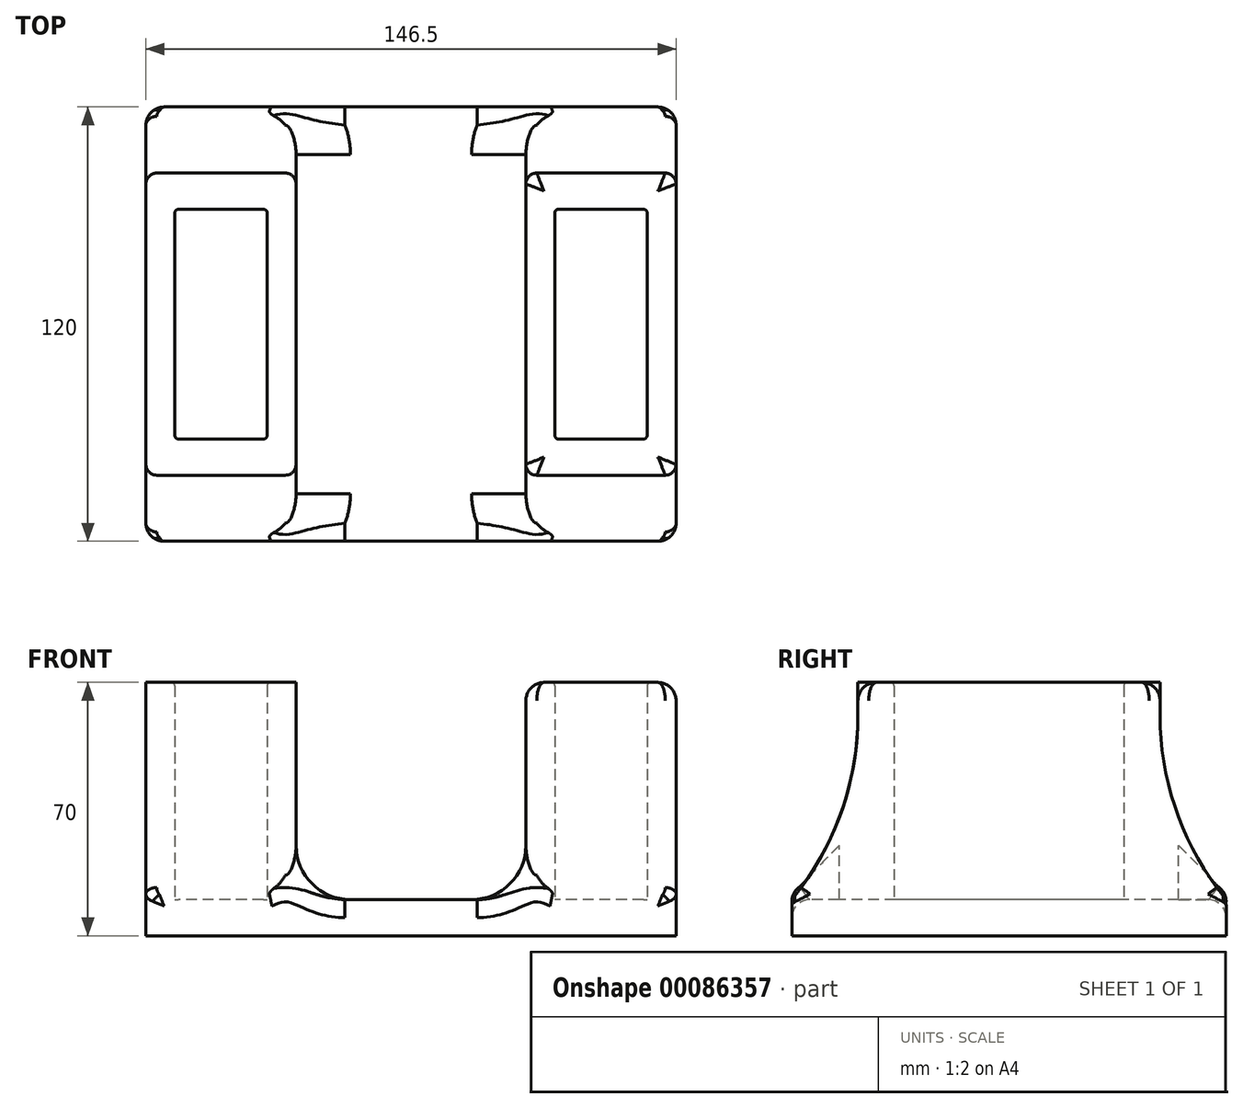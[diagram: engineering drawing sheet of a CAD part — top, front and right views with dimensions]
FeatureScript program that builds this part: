
annotation { "Feature Type Name" : "Feature", "Feature Type Description" : "" }
export const myFeature = defineFeature(function(context is Context, id is Id, definition is map)
    precondition{}
    {
        {
            var Q0;
            Q0=qCreatedBy(makeId("Top.planeOp"),FACE);
            var sketch = newSketch(context, id + "F0", { "sketchPlane" : qUnion([Q0])});
            skLineSegment(sketch, "E0.bottom", {"start": v(73.25, 60) * mm, "end": v(-73.25, 60) * mm});
            skLineSegment(sketch, "E0.top", {"start": v(73.25, -60) * mm, "end": v(-73.25, -60) * mm});
            skLineSegment(sketch, "E0.left", {"start": v(73.25, 60) * mm, "end": v(73.25, -60) * mm});
            skLineSegment(sketch, "E0.right", {"start": v(-73.25, 60) * mm, "end": v(-73.25, -60) * mm});
            skPoint(sketch, "E0.middle", {"position": v(0, 0) * mm});
            skLineSegment(sketch, "E1", {"start": v(-73.25, 0) * mm, "end": v(-52.5, 0) * mm});
            skPoint(sketch, "E1.endSnap0", {"position": v(-73.25, 0) * mm});
            skLineSegment(sketch, "E2", {"start": v(-52.5, 0) * mm, "end": v(52.5, 0) * mm});
            skPoint(sketch, "E2.endSnap0", {"position": v(73.25, 0) * mm});
            skLineSegment(sketch, "E3", {"start": v(52.5, 0) * mm, "end": v(73.25, 0) * mm});
            skLineSegment(sketch, "E4.bottom", {"start": v(-73.25, 41.75) * mm, "end": v(-31.75, 41.75) * mm});
            skLineSegment(sketch, "E4.top", {"start": v(-73.25, -41.75) * mm, "end": v(-31.75, -41.75) * mm});
            skLineSegment(sketch, "E4.left", {"start": v(-73.25, 41.75) * mm, "end": v(-73.25, -41.75) * mm});
            skLineSegment(sketch, "E4.right", {"start": v(-31.75, 41.75) * mm, "end": v(-31.75, -41.75) * mm});
            skPoint(sketch, "E4.middle", {"position": v(-52.5, 0) * mm});
            skLineSegment(sketch, "E5.bottom", {"start": v(73.25, 41.75) * mm, "end": v(31.75, 41.75) * mm});
            skLineSegment(sketch, "E5.top", {"start": v(73.25, -41.75) * mm, "end": v(31.75, -41.75) * mm});
            skLineSegment(sketch, "E5.left", {"start": v(73.25, 41.75) * mm, "end": v(73.25, -41.75) * mm});
            skLineSegment(sketch, "E5.right", {"start": v(31.75, 41.75) * mm, "end": v(31.75, -41.75) * mm});
            skPoint(sketch, "E5.middle", {"position": v(52.5, 0) * mm});
            skLineSegment(sketch, "E6.bottom", {"start": v(-39.75, 31.75) * mm, "end": v(-65.25, 31.75) * mm});
            skLineSegment(sketch, "E6.top", {"start": v(-39.75, -31.75) * mm, "end": v(-65.25, -31.75) * mm});
            skLineSegment(sketch, "E6.left", {"start": v(-39.75, 31.75) * mm, "end": v(-39.75, -31.75) * mm});
            skLineSegment(sketch, "E6.right", {"start": v(-65.25, 31.75) * mm, "end": v(-65.25, -31.75) * mm});
            skLineSegment(sketch, "E7.bottom", {"start": v(65.25, 31.75) * mm, "end": v(39.75, 31.75) * mm});
            skLineSegment(sketch, "E7.top", {"start": v(65.25, -31.75) * mm, "end": v(39.75, -31.75) * mm});
            skLineSegment(sketch, "E7.left", {"start": v(65.25, 31.75) * mm, "end": v(65.25, -31.75) * mm});
            skLineSegment(sketch, "E7.right", {"start": v(39.75, 31.75) * mm, "end": v(39.75, -31.75) * mm});
            skSolve(sketch);
        }
        {
            var Q0;
            {var subQ6=sQuery(id+"F0.wireOp",EDGE,"E0.top");Q0=makeQuery(id+"F0.imprint","IMPRINT",FACE,{"disambiguationData":[TD([[makeQuery(id+"F0.imprint","IMPRINT",EDGE,{"derivedFrom":subQ6}),-1.0]])]});}
            var Q1;
            {var subQ6=sQuery(id+"F0.wireOp",EDGE,"E0.bottom");Q1=makeQuery(id+"F0.imprint","IMPRINT",FACE,{"disambiguationData":[TD([[makeQuery(id+"F0.imprint","IMPRINT",EDGE,{"derivedFrom":subQ6}),1.0]])]});}
            var Q2;
            {var subQ3=sQuery(id+"F0.wireOp",EDGE,"E4.bottom");Q2=makeQuery(id+"F0.imprint","IMPRINT",FACE,{"disambiguationData":[TD([[makeQuery(id+"F0.imprint","IMPRINT",EDGE,{"derivedFrom":subQ3}),-1.0]])]});}
            var Q3;
            {var subQ3=sQuery(id+"F0.wireOp",EDGE,"E4.top");Q3=makeQuery(id+"F0.imprint","IMPRINT",FACE,{"disambiguationData":[TD([[makeQuery(id+"F0.imprint","IMPRINT",EDGE,{"derivedFrom":subQ3}),1.0]])]});}
            var Q4;
            {var subQ1=sQuery(id+"F0.wireOp",EDGE,"E6.top");Q4=makeQuery(id+"F0.imprint","IMPRINT",FACE,{"disambiguationData":[TD([[makeQuery(id+"F0.imprint","IMPRINT",EDGE,{"derivedFrom":subQ1}),-1.0]])]});}
            var Q5;
            {var subQ1=sQuery(id+"F0.wireOp",EDGE,"E6.bottom");Q5=makeQuery(id+"F0.imprint","IMPRINT",FACE,{"disambiguationData":[TD([[makeQuery(id+"F0.imprint","IMPRINT",EDGE,{"derivedFrom":subQ1}),1.0]])]});}
            var Q6;
            {var subQ1=sQuery(id+"F0.wireOp",EDGE,"E7.bottom");Q6=makeQuery(id+"F0.imprint","IMPRINT",FACE,{"disambiguationData":[TD([[makeQuery(id+"F0.imprint","IMPRINT",EDGE,{"derivedFrom":subQ1}),1.0]])]});}
            var Q7;
            {var subQ1=sQuery(id+"F0.wireOp",EDGE,"E7.top");Q7=makeQuery(id+"F0.imprint","IMPRINT",FACE,{"disambiguationData":[TD([[makeQuery(id+"F0.imprint","IMPRINT",EDGE,{"derivedFrom":subQ1}),-1.0]])]});}
            var Q8;
            {var subQ0=sQuery(id+"F0.wireOp",EDGE,"E5.top");Q8=makeQuery(id+"F0.imprint","IMPRINT",FACE,{"disambiguationData":[TD([[makeQuery(id+"F0.imprint","IMPRINT",EDGE,{"derivedFrom":subQ0}),-1.0]])]});}
            var Q9;
            {var subQ3=sQuery(id+"F0.wireOp",EDGE,"E5.bottom");Q9=makeQuery(id+"F0.imprint","IMPRINT",FACE,{"disambiguationData":[TD([[makeQuery(id+"F0.imprint","IMPRINT",EDGE,{"derivedFrom":subQ3}),1.0]])]});}
            extrude(context, id + "F1", {"entities" : qUnion([Q0, Q1, Q2, Q3, Q4, Q5, Q6, Q7, Q8, Q9]), "oppositeDirection" : true, "depth" : 10 * mm});
        }
        {
            var Q0;
            {var subQ3=sQuery(id+"F0.wireOp",EDGE,"E4.bottom");Q0=makeQuery(id+"F0.imprint","IMPRINT",FACE,{"disambiguationData":[TD([[makeQuery(id+"F0.imprint","IMPRINT",EDGE,{"derivedFrom":subQ3}),-1.0]])]});}
            var Q1;
            {var subQ3=sQuery(id+"F0.wireOp",EDGE,"E4.top");Q1=makeQuery(id+"F0.imprint","IMPRINT",FACE,{"disambiguationData":[TD([[makeQuery(id+"F0.imprint","IMPRINT",EDGE,{"derivedFrom":subQ3}),1.0]])]});}
            var Q2;
            {var subQ0=sQuery(id+"F0.wireOp",EDGE,"E5.top");Q2=makeQuery(id+"F0.imprint","IMPRINT",FACE,{"disambiguationData":[TD([[makeQuery(id+"F0.imprint","IMPRINT",EDGE,{"derivedFrom":subQ0}),-1.0]])]});}
            var Q3;
            {var subQ3=sQuery(id+"F0.wireOp",EDGE,"E5.bottom");Q3=makeQuery(id+"F0.imprint","IMPRINT",FACE,{"disambiguationData":[TD([[makeQuery(id+"F0.imprint","IMPRINT",EDGE,{"derivedFrom":subQ3}),1.0]])]});}
            extrude(context, id + "F2", {"entities" : qUnion([Q0, Q1, Q2, Q3]), "operationType" : NewBodyOperationType.ADD, "depth" : 60 * mm});
        }
        {
            var Q0;
            Q0=makeQuery(id+"F2.opExtrude","CAP_EDGE",EDGE,{"disambiguationData":[OSD([sQuery(id+"F0.wireOp",EDGE,"E4.top")])],"isStart":true});
            var Q1;
            Q1=makeQuery(id+"F2.opExtrude","CAP_EDGE",EDGE,{"disambiguationData":[OSD([sQuery(id+"F0.wireOp",EDGE,"E5.top")])],"isStart":true});
            var Q2;
            Q2=makeQuery(id+"F2.opExtrude","CAP_EDGE",EDGE,{"disambiguationData":[OSD([sQuery(id+"F0.wireOp",EDGE,"E5.bottom")])],"isStart":true});
            var Q3;
            Q3=makeQuery(id+"F2.opExtrude","CAP_EDGE",EDGE,{"disambiguationData":[OSD([sQuery(id+"F0.wireOp",EDGE,"E4.bottom")])],"isStart":true});
            fillet(context, id + "F3", {"entities" : qUnion([Q0, Q1, Q2, Q3]), "radius" : 80 * mm, "tangentPropagation" : true, "allowEdgeOverflow" : false});
        }
        {
            var Q0;
            Q0=makeQuery(id+"F2.opExtrude","SWEPT_EDGE",EDGE,{"disambiguationData":[OSD([sQuery(id+"F0.wireOp",EDGE,"E7.top"),sQuery(id+"F0.wireOp",EDGE,"E7.right")])]});
            var Q1;
            Q1=makeQuery(id+"F2.opExtrude","SWEPT_EDGE",EDGE,{"disambiguationData":[OSD([sQuery(id+"F0.wireOp",EDGE,"E7.top"),sQuery(id+"F0.wireOp",EDGE,"E7.left")])]});
            var Q2;
            Q2=makeQuery(id+"F2.opExtrude","SWEPT_EDGE",EDGE,{"disambiguationData":[OSD([sQuery(id+"F0.wireOp",EDGE,"E7.bottom"),sQuery(id+"F0.wireOp",EDGE,"E7.left")])]});
            var Q3;
            Q3=makeQuery(id+"F2.opExtrude","SWEPT_EDGE",EDGE,{"disambiguationData":[OSD([sQuery(id+"F0.wireOp",EDGE,"E7.bottom"),sQuery(id+"F0.wireOp",EDGE,"E7.right")])]});
            var Q4;
            Q4=makeQuery(id+"F2.opExtrude","SWEPT_EDGE",EDGE,{"disambiguationData":[OSD([sQuery(id+"F0.wireOp",EDGE,"E6.bottom"),sQuery(id+"F0.wireOp",EDGE,"E6.right")])]});
            var Q5;
            Q5=makeQuery(id+"F2.opExtrude","SWEPT_EDGE",EDGE,{"disambiguationData":[OSD([sQuery(id+"F0.wireOp",EDGE,"E6.bottom"),sQuery(id+"F0.wireOp",EDGE,"E6.left")])]});
            var Q6;
            Q6=makeQuery(id+"F2.opExtrude","SWEPT_EDGE",EDGE,{"disambiguationData":[OSD([sQuery(id+"F0.wireOp",EDGE,"E6.top"),sQuery(id+"F0.wireOp",EDGE,"E6.left")])]});
            var Q7;
            Q7=makeQuery(id+"F2.opExtrude","SWEPT_EDGE",EDGE,{"disambiguationData":[OSD([sQuery(id+"F0.wireOp",EDGE,"E6.top"),sQuery(id+"F0.wireOp",EDGE,"E6.right")])]});
            fillet(context, id + "F4", {"entities" : qUnion([Q0, Q1, Q2, Q3, Q4, Q5, Q6, Q7]), "radius" : 1 * mm, "tangentPropagation" : true, "allowEdgeOverflow" : false});
        }
        {
            var Q0;
            {var subQ0=sQuery(id+"F0.wireOp",EDGE,"E5.left");Q0=makeQuery(id+"F3.opFillet","BLEND_EDGE",EDGE,{"blendedFrom":[makeQuery(id+"F2.opExtrude","CAP_EDGE",EDGE,{"disambiguationData":[OSD([sQuery(id+"F0.wireOp",EDGE,"E5.bottom")])],"isStart":true}),makeQuery(id+"F2.boolean.opBoolean","MERGE",FACE,{"derivedFrom":[makeQuery(id+"F1.opExtrude","SWEPT_FACE",FACE,{"disambiguationData":[OSD([sQuery(id+"F0.wireOp",EDGE,"E0.left"),subQ0])]}),makeQuery(id+"F2.opExtrude","SWEPT_FACE",FACE,{"disambiguationData":[OSD([subQ0])]})]})],"blendedInto":[makeQuery(id+"F2.boolean.opBoolean","MERGE",FACE,{"derivedFrom":[makeQuery(id+"F1.opExtrude","SWEPT_FACE",FACE,{"disambiguationData":[OSD([sQuery(id+"F0.wireOp",EDGE,"E0.left"),subQ0])]}),makeQuery(id+"F2.opExtrude","SWEPT_FACE",FACE,{"disambiguationData":[OSD([subQ0])]})]})]});}
            var Q1;
            Q1=makeQuery(id+"F3.opFillet","BLEND_EDGE",EDGE,{"blendedFrom":[makeQuery(id+"F2.opExtrude","CAP_EDGE",EDGE,{"disambiguationData":[OSD([sQuery(id+"F0.wireOp",EDGE,"E5.bottom")])],"isStart":true}),makeQuery(id+"F2.opExtrude","SWEPT_FACE",FACE,{"disambiguationData":[OSD([sQuery(id+"F0.wireOp",EDGE,"E5.right")])]})],"blendedInto":[makeQuery(id+"F2.opExtrude","SWEPT_FACE",FACE,{"disambiguationData":[OSD([sQuery(id+"F0.wireOp",EDGE,"E5.right")])]})]});
            var Q2;
            Q2=makeQuery(id+"F3.opFillet","BLEND_EDGE",EDGE,{"blendedFrom":[makeQuery(id+"F2.opExtrude","CAP_EDGE",EDGE,{"disambiguationData":[OSD([sQuery(id+"F0.wireOp",EDGE,"E4.bottom")])],"isStart":true}),makeQuery(id+"F2.opExtrude","SWEPT_FACE",FACE,{"disambiguationData":[OSD([sQuery(id+"F0.wireOp",EDGE,"E4.right")])]})],"blendedInto":[makeQuery(id+"F2.opExtrude","SWEPT_FACE",FACE,{"disambiguationData":[OSD([sQuery(id+"F0.wireOp",EDGE,"E4.right")])]})]});
            var Q3;
            {var subQ0=sQuery(id+"F0.wireOp",EDGE,"E4.left");Q3=makeQuery(id+"F3.opFillet","BLEND_EDGE",EDGE,{"blendedFrom":[makeQuery(id+"F2.opExtrude","CAP_EDGE",EDGE,{"disambiguationData":[OSD([sQuery(id+"F0.wireOp",EDGE,"E4.bottom")])],"isStart":true}),makeQuery(id+"F2.boolean.opBoolean","MERGE",FACE,{"derivedFrom":[makeQuery(id+"F1.opExtrude","SWEPT_FACE",FACE,{"disambiguationData":[OSD([sQuery(id+"F0.wireOp",EDGE,"E0.right"),subQ0])]}),makeQuery(id+"F2.opExtrude","SWEPT_FACE",FACE,{"disambiguationData":[OSD([subQ0])]})]})],"blendedInto":[makeQuery(id+"F2.boolean.opBoolean","MERGE",FACE,{"derivedFrom":[makeQuery(id+"F1.opExtrude","SWEPT_FACE",FACE,{"disambiguationData":[OSD([sQuery(id+"F0.wireOp",EDGE,"E0.right"),subQ0])]}),makeQuery(id+"F2.opExtrude","SWEPT_FACE",FACE,{"disambiguationData":[OSD([subQ0])]})]})]});}
            var Q4;
            Q4=makeQuery(id+"F3.opFillet","BLEND_EDGE",EDGE,{"blendedFrom":[makeQuery(id+"F2.opExtrude","CAP_EDGE",EDGE,{"disambiguationData":[OSD([sQuery(id+"F0.wireOp",EDGE,"E4.top")])],"isStart":true}),makeQuery(id+"F2.opExtrude","SWEPT_FACE",FACE,{"disambiguationData":[OSD([sQuery(id+"F0.wireOp",EDGE,"E4.right")])]})],"blendedInto":[makeQuery(id+"F2.opExtrude","SWEPT_FACE",FACE,{"disambiguationData":[OSD([sQuery(id+"F0.wireOp",EDGE,"E4.right")])]})]});
            var Q5;
            {var subQ0=sQuery(id+"F0.wireOp",EDGE,"E5.left");Q5=makeQuery(id+"F3.opFillet","BLEND_EDGE",EDGE,{"blendedFrom":[makeQuery(id+"F2.opExtrude","CAP_EDGE",EDGE,{"disambiguationData":[OSD([sQuery(id+"F0.wireOp",EDGE,"E5.top")])],"isStart":true}),makeQuery(id+"F2.boolean.opBoolean","MERGE",FACE,{"derivedFrom":[makeQuery(id+"F1.opExtrude","SWEPT_FACE",FACE,{"disambiguationData":[OSD([sQuery(id+"F0.wireOp",EDGE,"E0.left"),subQ0])]}),makeQuery(id+"F2.opExtrude","SWEPT_FACE",FACE,{"disambiguationData":[OSD([subQ0])]})]})],"blendedInto":[makeQuery(id+"F2.boolean.opBoolean","MERGE",FACE,{"derivedFrom":[makeQuery(id+"F1.opExtrude","SWEPT_FACE",FACE,{"disambiguationData":[OSD([sQuery(id+"F0.wireOp",EDGE,"E0.left"),subQ0])]}),makeQuery(id+"F2.opExtrude","SWEPT_FACE",FACE,{"disambiguationData":[OSD([subQ0])]})]})]});}
            var Q6;
            {var subQ0=sQuery(id+"F0.wireOp",EDGE,"E4.left");Q6=makeQuery(id+"F3.opFillet","BLEND_EDGE",EDGE,{"blendedFrom":[makeQuery(id+"F2.opExtrude","CAP_EDGE",EDGE,{"disambiguationData":[OSD([sQuery(id+"F0.wireOp",EDGE,"E4.top")])],"isStart":true}),makeQuery(id+"F2.boolean.opBoolean","MERGE",FACE,{"derivedFrom":[makeQuery(id+"F1.opExtrude","SWEPT_FACE",FACE,{"disambiguationData":[OSD([sQuery(id+"F0.wireOp",EDGE,"E0.right"),subQ0])]}),makeQuery(id+"F2.opExtrude","SWEPT_FACE",FACE,{"disambiguationData":[OSD([subQ0])]})]})],"blendedInto":[makeQuery(id+"F2.boolean.opBoolean","MERGE",FACE,{"derivedFrom":[makeQuery(id+"F1.opExtrude","SWEPT_FACE",FACE,{"disambiguationData":[OSD([sQuery(id+"F0.wireOp",EDGE,"E0.right"),subQ0])]}),makeQuery(id+"F2.opExtrude","SWEPT_FACE",FACE,{"disambiguationData":[OSD([subQ0])]})]})]});}
            var Q7;
            Q7=makeQuery(id+"F3.opFillet","BLEND_EDGE",EDGE,{"blendedFrom":[makeQuery(id+"F2.opExtrude","CAP_EDGE",EDGE,{"disambiguationData":[OSD([sQuery(id+"F0.wireOp",EDGE,"E5.top")])],"isStart":true}),makeQuery(id+"F2.opExtrude","SWEPT_FACE",FACE,{"disambiguationData":[OSD([sQuery(id+"F0.wireOp",EDGE,"E5.right")])]})],"blendedInto":[makeQuery(id+"F2.opExtrude","SWEPT_FACE",FACE,{"disambiguationData":[OSD([sQuery(id+"F0.wireOp",EDGE,"E5.right")])]})]});
            fillet(context, id + "F5", {"entities" : qUnion([Q0, Q1, Q2, Q3, Q4, Q5, Q6, Q7]), "radius" : 3 * mm, "tangentPropagation" : true, "allowEdgeOverflow" : false});
        }
        {
            var Q0;
            Q0=makeQuery(id+"F2.opExtrude","CAP_EDGE",EDGE,{"disambiguationData":[OSD([sQuery(id+"F0.wireOp",EDGE,"E5.right")])],"isStart":false});
            var Q1;
            Q1=makeQuery(id+"F2.opExtrude","CAP_EDGE",EDGE,{"disambiguationData":[OSD([sQuery(id+"F0.wireOp",EDGE,"E4.left")])],"isStart":false});
            fillet(context, id + "F6", {"entities" : qUnion([Q0, Q1]), "radius" : 5 * mm, "tangentPropagation" : true, "allowEdgeOverflow" : false});
        }
        {
            var Q0;
            Q0=makeQuery(id+"F2.opExtrude","CAP_EDGE",EDGE,{"disambiguationData":[OSD([sQuery(id+"F0.wireOp",EDGE,"E7.top")])],"isStart":false});
            var Q1;
            Q1=makeQuery(id+"F2.opExtrude","CAP_EDGE",EDGE,{"disambiguationData":[OSD([sQuery(id+"F0.wireOp",EDGE,"E6.top")])],"isStart":false});
            fillet(context, id + "F7", {"entities" : qUnion([Q0, Q1]), "radius" : 1 * mm, "tangentPropagation" : true, "allowEdgeOverflow" : false});
        }
        {
            var Q0;
            Q0=makeQuery(id+"F2.opExtrude","CAP_EDGE",EDGE,{"disambiguationData":[OSD([sQuery(id+"F0.wireOp",EDGE,"E4.right")])],"isStart":true});
            var Q1;
            Q1=makeQuery(id+"F2.opExtrude","CAP_EDGE",EDGE,{"disambiguationData":[OSD([sQuery(id+"F0.wireOp",EDGE,"E5.right")])],"isStart":true});
            fillet(context, id + "F8", {"entities" : qUnion([Q0, Q1]), "radius" : 15 * mm, "tangentPropagation" : true, "allowEdgeOverflow" : false});
        }
        {
            var Q0;
            Q0=makeQuery(id+"F3.opFillet","BLEND_EDGE",EDGE,{"blendedFrom":[makeQuery(id+"F2.opExtrude","CAP_EDGE",EDGE,{"disambiguationData":[OSD([sQuery(id+"F0.wireOp",EDGE,"E5.bottom")])],"isStart":true}),makeQuery(id+"F1.opExtrude","SWEPT_FACE",FACE,{"disambiguationData":[OSD([sQuery(id+"F0.wireOp",EDGE,"E0.bottom")])]})],"blendedInto":[makeQuery(id+"F1.opExtrude","SWEPT_FACE",FACE,{"disambiguationData":[OSD([sQuery(id+"F0.wireOp",EDGE,"E0.bottom")])]})]});
            var Q1;
            {var subQ0=sQuery(id+"F0.wireOp",EDGE,"E0.bottom");var subQ1=makeQuery(id+"F1.opExtrude","SWEPT_FACE",FACE,{"disambiguationData":[OSD([subQ0])]});var subQ2=sQuery(id+"F0.wireOp",EDGE,"E5.bottom");var subQ3=sQuery(id+"F0.wireOp",EDGE,"E5.left");var subQ4=sQuery(id+"F0.wireOp",EDGE,"E0.left");var subQ5=sQuery(id+"F0.wireOp",EDGE,"E4.left");var subQ6=sQuery(id+"F0.wireOp",EDGE,"E0.top");var subQ7=sQuery(id+"F0.wireOp",EDGE,"E0.right");var subQ8=makeQuery(id+"F2.opExtrude","SWEPT_FACE",FACE,{"disambiguationData":[OSD([sQuery(id+"F0.wireOp",EDGE,"E5.right")])]});Q1=makeQuery(id+"F8.opFillet","BLEND_EDGE",EDGE,{"blendedFrom":[makeQuery(id+"F5.opFillet","BLEND_EDGE",EDGE,{"blendedFrom":[makeQuery(id+"F3.opFillet","BLEND_EDGE",EDGE,{"blendedFrom":[makeQuery(id+"F2.opExtrude","CAP_EDGE",EDGE,{"disambiguationData":[OSD([subQ2])],"isStart":true}),subQ8],"blendedInto":[subQ8]}),makeQuery(id+"F2.boolean.opBoolean","SPLIT",FACE,{"disambiguationData":[TD([subQ1])],"derivedFrom":makeQuery(id+"F1.opExtrude","CAP_FACE",FACE,{"disambiguationData":[OSD([subQ0,subQ6,subQ4,subQ7,subQ5,subQ3])],"isStart":true})})],"blendedInto":[makeQuery(id+"F2.boolean.opBoolean","SPLIT",FACE,{"disambiguationData":[TD([subQ1])],"derivedFrom":makeQuery(id+"F1.opExtrude","CAP_FACE",FACE,{"disambiguationData":[OSD([subQ0,subQ6,subQ4,subQ7,subQ5,subQ3])],"isStart":true})})]}),subQ1],"blendedInto":[subQ1]});}
            var Q2;
            Q2=makeQuery(id+"F1.opExtrude","CAP_EDGE",EDGE,{"disambiguationData":[OSD([sQuery(id+"F0.wireOp",EDGE,"E0.bottom")])],"isStart":true});
            var Q3;
            {var subQ0=sQuery(id+"F0.wireOp",EDGE,"E0.bottom");var subQ1=makeQuery(id+"F1.opExtrude","SWEPT_FACE",FACE,{"disambiguationData":[OSD([subQ0])]});var subQ2=sQuery(id+"F0.wireOp",EDGE,"E5.left");var subQ3=sQuery(id+"F0.wireOp",EDGE,"E0.left");var subQ4=makeQuery(id+"F2.opExtrude","SWEPT_FACE",FACE,{"disambiguationData":[OSD([sQuery(id+"F0.wireOp",EDGE,"E4.right")])]});var subQ5=sQuery(id+"F0.wireOp",EDGE,"E4.left");var subQ6=sQuery(id+"F0.wireOp",EDGE,"E4.bottom");var subQ7=sQuery(id+"F0.wireOp",EDGE,"E0.top");var subQ8=sQuery(id+"F0.wireOp",EDGE,"E0.right");Q3=makeQuery(id+"F8.opFillet","BLEND_EDGE",EDGE,{"blendedFrom":[makeQuery(id+"F5.opFillet","BLEND_EDGE",EDGE,{"blendedFrom":[makeQuery(id+"F3.opFillet","BLEND_EDGE",EDGE,{"blendedFrom":[makeQuery(id+"F2.opExtrude","CAP_EDGE",EDGE,{"disambiguationData":[OSD([subQ6])],"isStart":true}),subQ4],"blendedInto":[subQ4]}),makeQuery(id+"F2.boolean.opBoolean","SPLIT",FACE,{"disambiguationData":[TD([subQ1])],"derivedFrom":makeQuery(id+"F1.opExtrude","CAP_FACE",FACE,{"disambiguationData":[OSD([subQ0,subQ7,subQ3,subQ8,subQ5,subQ2])],"isStart":true})})],"blendedInto":[makeQuery(id+"F2.boolean.opBoolean","SPLIT",FACE,{"disambiguationData":[TD([subQ1])],"derivedFrom":makeQuery(id+"F1.opExtrude","CAP_FACE",FACE,{"disambiguationData":[OSD([subQ0,subQ7,subQ3,subQ8,subQ5,subQ2])],"isStart":true})})]}),subQ1],"blendedInto":[subQ1]});}
            var Q4;
            Q4=makeQuery(id+"F3.opFillet","BLEND_EDGE",EDGE,{"blendedFrom":[makeQuery(id+"F2.opExtrude","CAP_EDGE",EDGE,{"disambiguationData":[OSD([sQuery(id+"F0.wireOp",EDGE,"E4.bottom")])],"isStart":true}),makeQuery(id+"F1.opExtrude","SWEPT_FACE",FACE,{"disambiguationData":[OSD([sQuery(id+"F0.wireOp",EDGE,"E0.bottom")])]})],"blendedInto":[makeQuery(id+"F1.opExtrude","SWEPT_FACE",FACE,{"disambiguationData":[OSD([sQuery(id+"F0.wireOp",EDGE,"E0.bottom")])]})]});
            var Q5;
            Q5=makeQuery(id+"F1.opExtrude","CAP_EDGE",EDGE,{"disambiguationData":[OSD([sQuery(id+"F0.wireOp",EDGE,"E0.top")])],"isStart":true});
            var Q6;
            {var subQ0=sQuery(id+"F0.wireOp",EDGE,"E0.top");var subQ1=makeQuery(id+"F1.opExtrude","SWEPT_FACE",FACE,{"disambiguationData":[OSD([subQ0])]});var subQ2=sQuery(id+"F0.wireOp",EDGE,"E5.left");var subQ3=sQuery(id+"F0.wireOp",EDGE,"E0.left");var subQ4=makeQuery(id+"F2.opExtrude","SWEPT_FACE",FACE,{"disambiguationData":[OSD([sQuery(id+"F0.wireOp",EDGE,"E4.right")])]});var subQ5=sQuery(id+"F0.wireOp",EDGE,"E4.left");var subQ6=sQuery(id+"F0.wireOp",EDGE,"E0.bottom");var subQ7=sQuery(id+"F0.wireOp",EDGE,"E4.top");var subQ8=sQuery(id+"F0.wireOp",EDGE,"E0.right");Q6=makeQuery(id+"F8.opFillet","BLEND_EDGE",EDGE,{"blendedFrom":[makeQuery(id+"F5.opFillet","BLEND_EDGE",EDGE,{"blendedFrom":[makeQuery(id+"F3.opFillet","BLEND_EDGE",EDGE,{"blendedFrom":[makeQuery(id+"F2.opExtrude","CAP_EDGE",EDGE,{"disambiguationData":[OSD([subQ7])],"isStart":true}),subQ4],"blendedInto":[subQ4]}),makeQuery(id+"F2.boolean.opBoolean","SPLIT",FACE,{"disambiguationData":[TD([makeQuery(id+"F1.opExtrude","SWEPT_FACE",FACE,{"disambiguationData":[OSD([subQ6])]})])],"derivedFrom":makeQuery(id+"F1.opExtrude","CAP_FACE",FACE,{"disambiguationData":[OSD([subQ6,subQ0,subQ3,subQ8,subQ5,subQ2])],"isStart":true})})],"blendedInto":[makeQuery(id+"F2.boolean.opBoolean","SPLIT",FACE,{"disambiguationData":[TD([makeQuery(id+"F1.opExtrude","SWEPT_FACE",FACE,{"disambiguationData":[OSD([subQ6])]})])],"derivedFrom":makeQuery(id+"F1.opExtrude","CAP_FACE",FACE,{"disambiguationData":[OSD([subQ6,subQ0,subQ3,subQ8,subQ5,subQ2])],"isStart":true})})]}),subQ1],"blendedInto":[subQ1]});}
            var Q7;
            {var subQ0=sQuery(id+"F0.wireOp",EDGE,"E0.top");var subQ1=makeQuery(id+"F1.opExtrude","SWEPT_FACE",FACE,{"disambiguationData":[OSD([subQ0])]});var subQ2=sQuery(id+"F0.wireOp",EDGE,"E5.top");var subQ3=sQuery(id+"F0.wireOp",EDGE,"E5.left");var subQ4=sQuery(id+"F0.wireOp",EDGE,"E0.left");var subQ5=sQuery(id+"F0.wireOp",EDGE,"E4.left");var subQ6=sQuery(id+"F0.wireOp",EDGE,"E0.bottom");var subQ7=sQuery(id+"F0.wireOp",EDGE,"E0.right");var subQ8=makeQuery(id+"F2.opExtrude","SWEPT_FACE",FACE,{"disambiguationData":[OSD([sQuery(id+"F0.wireOp",EDGE,"E5.right")])]});Q7=makeQuery(id+"F8.opFillet","BLEND_EDGE",EDGE,{"blendedFrom":[makeQuery(id+"F5.opFillet","BLEND_EDGE",EDGE,{"blendedFrom":[makeQuery(id+"F3.opFillet","BLEND_EDGE",EDGE,{"blendedFrom":[makeQuery(id+"F2.opExtrude","CAP_EDGE",EDGE,{"disambiguationData":[OSD([subQ2])],"isStart":true}),subQ8],"blendedInto":[subQ8]}),makeQuery(id+"F2.boolean.opBoolean","SPLIT",FACE,{"disambiguationData":[TD([makeQuery(id+"F1.opExtrude","SWEPT_FACE",FACE,{"disambiguationData":[OSD([subQ6])]})])],"derivedFrom":makeQuery(id+"F1.opExtrude","CAP_FACE",FACE,{"disambiguationData":[OSD([subQ6,subQ0,subQ4,subQ7,subQ5,subQ3])],"isStart":true})})],"blendedInto":[makeQuery(id+"F2.boolean.opBoolean","SPLIT",FACE,{"disambiguationData":[TD([makeQuery(id+"F1.opExtrude","SWEPT_FACE",FACE,{"disambiguationData":[OSD([subQ6])]})])],"derivedFrom":makeQuery(id+"F1.opExtrude","CAP_FACE",FACE,{"disambiguationData":[OSD([subQ6,subQ0,subQ4,subQ7,subQ5,subQ3])],"isStart":true})})]}),subQ1],"blendedInto":[subQ1]});}
            var Q8;
            Q8=makeQuery(id+"F3.opFillet","BLEND_EDGE",EDGE,{"blendedFrom":[makeQuery(id+"F2.opExtrude","CAP_EDGE",EDGE,{"disambiguationData":[OSD([sQuery(id+"F0.wireOp",EDGE,"E5.top")])],"isStart":true}),makeQuery(id+"F1.opExtrude","SWEPT_FACE",FACE,{"disambiguationData":[OSD([sQuery(id+"F0.wireOp",EDGE,"E0.top")])]})],"blendedInto":[makeQuery(id+"F1.opExtrude","SWEPT_FACE",FACE,{"disambiguationData":[OSD([sQuery(id+"F0.wireOp",EDGE,"E0.top")])]})]});
            var Q9;
            Q9=makeQuery(id+"F3.opFillet","BLEND_EDGE",EDGE,{"blendedFrom":[makeQuery(id+"F2.opExtrude","CAP_EDGE",EDGE,{"disambiguationData":[OSD([sQuery(id+"F0.wireOp",EDGE,"E4.top")])],"isStart":true}),makeQuery(id+"F1.opExtrude","SWEPT_FACE",FACE,{"disambiguationData":[OSD([sQuery(id+"F0.wireOp",EDGE,"E0.top")])]})],"blendedInto":[makeQuery(id+"F1.opExtrude","SWEPT_FACE",FACE,{"disambiguationData":[OSD([sQuery(id+"F0.wireOp",EDGE,"E0.top")])]})]});
            fillet(context, id + "F9", {"entities" : qUnion([Q0, Q1, Q2, Q3, Q4, Q5, Q6, Q7, Q8, Q9]), "radius" : 5 * mm, "tangentPropagation" : true, "allowEdgeOverflow" : false});
        }
    });
